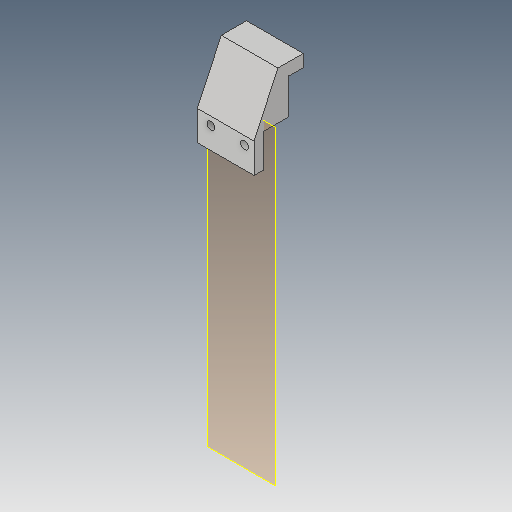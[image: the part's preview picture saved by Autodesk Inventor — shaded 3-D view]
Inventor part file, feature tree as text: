
AUTODESK INVENTOR PART (.ipt)
format: ipt  version: 2019.4 (Build 234330000, 330)  size: 146,432 bytes
history: native  units: mm
features: reference x6, extrude x5, sketch x5, other x5, plane x2, projected_geometry x2, chamfer x1
ambient origin geometry x8: Origin, YZ Plane, XZ Plane, XY Plane, X Axis, Y Axis, Z Axis, Center Point
bodies: Solid1 (feature_tree)
feature tree (26):
  plane  "Work Plane1"
  extrude  "Extrusion1"  Depth=4.0mm TaperAngle=0.0deg
  sketch  "Sketch2"  dims[d4=6.0mm d5=0.0mm d6=2.0mm d7=0.0mm]
  plane  "Work Plane2"
  extrude  "Extrusion2"  Depth=2.0mm TaperAngle=0.0deg
  extrude  "Extrusion3"  Depth=10.0mm
  extrude  "Extrusion4"  [1 undecoded]
  extrude  "Extrusion5"  [1 undecoded]
  chamfer  "Chamfer1"  [1 undecoded]
  sketch  "Sketch1"  dims[d0=4.0mm d1=0.0mm d2=4.0mm d3=0.0mm]
  reference  "Reference1"
  projected_geometry  "Projected Loop1"
  sketch  "Sketch3"  dims[d8=2.0mm d9=0.0mm d10=10.0mm d11=2.0mm d12=11.34464mm]
  projected_geometry  "Projected Loop2"
  reference  "Reference2"
  sketch  "Sketch4"
  reference  "Reference3"
  reference  "Reference4"
  reference  "Reference5"
  sketch  "Sketch5"
  reference  "Reference6"
  other  "Assembly_Opentrons_Autofocus_v1.iam"
  other  "01_Slide_camera_x_v1:1"
  other  "00_NEMA11:1"
  other  "Lagerschild_11_1"
  other  "Stator_11_8"
note: 3 required parameter values undecoded (feature->parameter linkage not recoverable at this tier; creation-order binding heuristic only, values carry confidence <= 0.55)
